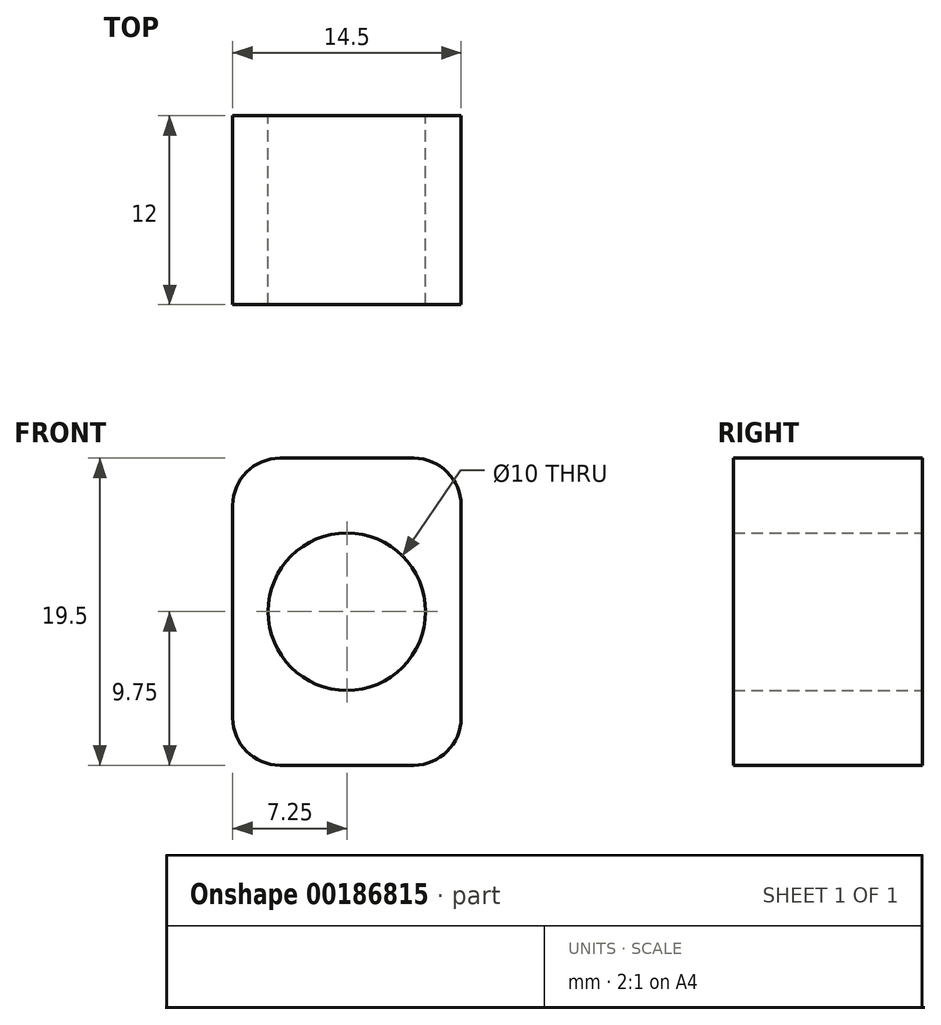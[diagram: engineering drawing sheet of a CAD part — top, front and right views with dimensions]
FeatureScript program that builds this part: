
annotation { "Feature Type Name" : "Feature", "Feature Type Description" : "" }
export const myFeature = defineFeature(function(context is Context, id is Id, definition is map)
    precondition{}
    {
        {
            var Q0;
            Q0=qCreatedBy(makeId("Front.planeOp"),FACE);
            var sketch = newSketch(context, id + "F0", { "sketchPlane" : qUnion([Q0])});
            skLineSegment(sketch, "E0.bottom", {"start": v(-7.25, 9.75) * mm, "end": v(7.25, 9.75) * mm});
            skLineSegment(sketch, "E0.top", {"start": v(-7.25, -9.75) * mm, "end": v(7.25, -9.75) * mm});
            skLineSegment(sketch, "E0.left", {"start": v(-7.25, 9.75) * mm, "end": v(-7.25, -9.75) * mm});
            skLineSegment(sketch, "E0.right", {"start": v(7.25, 9.75) * mm, "end": v(7.25, -9.75) * mm});
            skPoint(sketch, "E0.middle", {"position": v(0, 0) * mm});
            skCircle(sketch, "E1", {"center": v(0, 0) * mm, "radius": 5 * mm});
            skSolve(sketch);
        }
        {
            var Q0;
            Q0=makeQuery(id+"F0.imprint","IMPRINT",FACE,{"disambiguationData":[TD([[makeQuery(id+"F0.imprint","IMPRINT",EDGE,{"derivedFrom":sQuery(id+"F0.wireOp",EDGE,"E0.bottom")}),-1.0]])]});
            extrude(context, id + "F1", {"entities" : qUnion([Q0]), "depth" : 12 * mm});
        }
        {
            var Q0;
            Q0=makeQuery(id+"F1.opExtrude","SWEPT_EDGE",EDGE,{"disambiguationData":[OSD([sQuery(id+"F0.wireOp",EDGE,"E0.bottom"),sQuery(id+"F0.wireOp",EDGE,"E0.left")])]});
            var Q1;
            Q1=makeQuery(id+"F1.opExtrude","SWEPT_EDGE",EDGE,{"disambiguationData":[OSD([sQuery(id+"F0.wireOp",EDGE,"E0.bottom"),sQuery(id+"F0.wireOp",EDGE,"E0.right")])]});
            var Q2;
            Q2=makeQuery(id+"F1.opExtrude","SWEPT_EDGE",EDGE,{"disambiguationData":[OSD([sQuery(id+"F0.wireOp",EDGE,"E0.top"),sQuery(id+"F0.wireOp",EDGE,"E0.right")])]});
            var Q3;
            Q3=makeQuery(id+"F1.opExtrude","SWEPT_EDGE",EDGE,{"disambiguationData":[OSD([sQuery(id+"F0.wireOp",EDGE,"E0.top"),sQuery(id+"F0.wireOp",EDGE,"E0.left")])]});
            fillet(context, id + "F2", {"entities" : qUnion([Q0, Q1, Q2, Q3]), "radius" : 3 * mm, "tangentPropagation" : true, "allowEdgeOverflow" : false});
        }
    });
